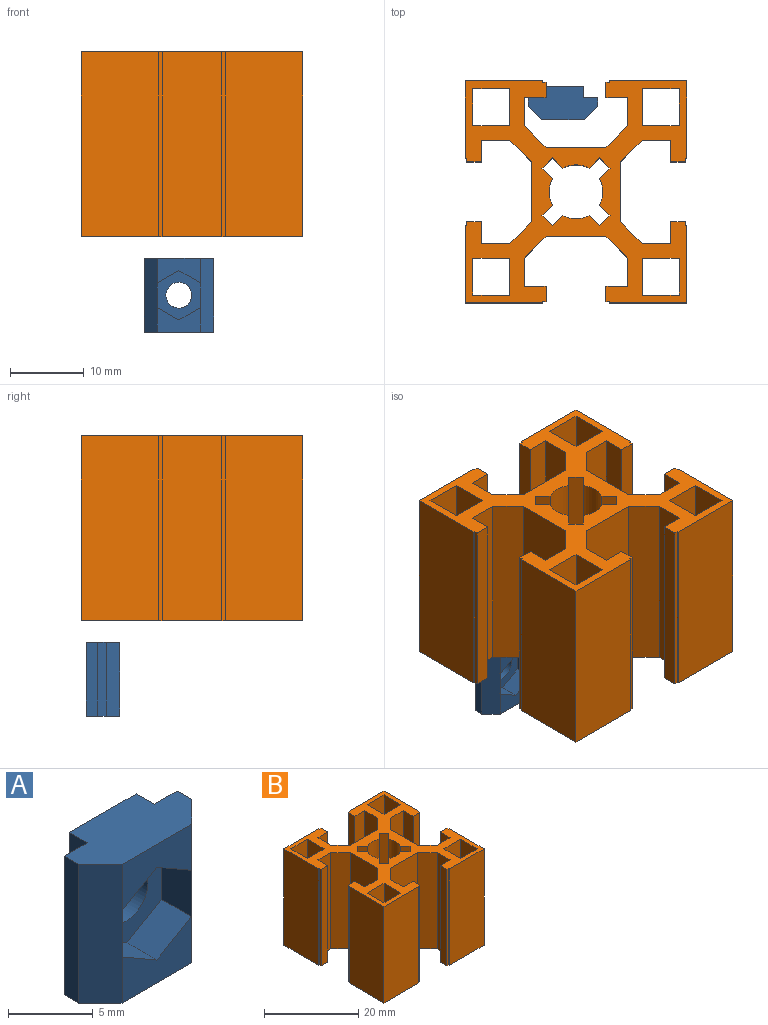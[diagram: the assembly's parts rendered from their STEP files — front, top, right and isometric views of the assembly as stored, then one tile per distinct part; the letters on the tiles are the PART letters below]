
ASSEMBLY  parts=2 mates=1
PART A: 21 faces, bbox 9.4x4.5x10 mm
  f0: plane 5.8x3.33mm, normal (0,-1,0), area 14.4mm2, adj f6,f8,f13,f17,f18
  f1: cylinder r=1.75mm len=3.5mm, axis (0,1,0), area 22mm2, adj f2,f14
  f2: plane 10x5.55mm, normal (0,1,0), area 45.9mm2, adj f1,f3,f11,f12,f13
  f3: plane 10x1.5mm, normal (-1,0.02,0), area 15mm2, adj f2,f4,f12,f13
  f4: plane 10x1.9mm, normal (0,1,0), area 19mm2, adj f3,f5,f12,f13
  f5: plane 10x1.2mm, normal (-1,0,0), area 12mm2, adj f4,f6,f12,f13
  f6: plane 10x1.8mm, normal (-0.71,-0.71,0), area 25.5mm2, adj f0,f5,f7,f12,f13,f16
  f7: plane 5.8x3.33mm, normal (0,-1,0), area 14.4mm2, adj f6,f8,f12,f15,f20
  f8: plane 10x1.8mm, normal (0.71,-0.71,0), area 25.5mm2, adj f0,f7,f9,f12,f13,f19
  f9: plane 10x1.2mm, normal (1,0,0), area 12mm2, adj f8,f10,f12,f13
  f10: plane 10x1.9mm, normal (0,1,0), area 19mm2, adj f9,f11,f12,f13
  f11: plane 10x1.5mm, normal (1,0.02,0), area 15mm2, adj f2,f10,f12,f13
  f12: plane 9.4x4.5mm, normal (0,0,1), area 33.3mm2, adj f2,f3,f4,f5,f6,f7,f8,f9
  f13: plane 9.4x4.5mm, normal (0,0,-1), area 33.3mm2, adj f0,f2,f3,f4,f5,f6,f8,f9
  f14: plane 6.7x5.8mm, normal (0,-1,0), area 19.5mm2, adj f1,f15,f16,f17,f18,f19,f20
  f15: plane 2.9x2.5mm, normal (0.5,0,-0.87), area 8.4mm2, adj f7,f14,f16,f20
  f16: plane 3.35x2.5mm, normal (1,0,0), area 8.4mm2, adj f6,f14,f15,f17
  f17: plane 2.9x2.5mm, normal (0.5,0,0.87), area 8.4mm2, adj f0,f14,f16,f18
  f18: plane 2.9x2.5mm, normal (-0.5,0,0.87), area 8.4mm2, adj f0,f14,f17,f19
  f19: plane 3.35x2.5mm, normal (-1,0,0), area 8.4mm2, adj f8,f14,f18,f20
  f20: plane 2.9x2.5mm, normal (-0.5,0,-0.87), area 8.4mm2, adj f7,f14,f15,f19
PART B: 94 faces, bbox 30x30x25 mm
  f0: cylinder r=3.65mm len=25mm, axis (0,0,-1), area 92.7mm2, adj f1,f91,f92,f93
  f1: plane 25x1.41mm, normal (0.71,-0.71,0), area 50mm2, adj f0,f2,f92,f93
  f2: plane 25x1.41mm, normal (-0.71,-0.71,0), area 50mm2, adj f1,f3,f92,f93
  f3: plane 25x1.41mm, normal (-0.71,0.71,0), area 50mm2, adj f2,f4,f92,f93
  f4: cylinder r=3.65mm len=25mm, axis (0,0,-1), area 92.7mm2, adj f3,f5,f92,f93
  f5: plane 25x1.41mm, normal (-0.71,-0.71,0), area 50mm2, adj f4,f6,f92,f93
  f6: plane 25x1.41mm, normal (-0.71,0.71,0), area 50mm2, adj f5,f7,f92,f93
  f7: plane 25x1.41mm, normal (0.71,0.71,0), area 50mm2, adj f6,f8,f92,f93
  f8: cylinder r=3.65mm len=25mm, axis (0,0,-1), area 92.7mm2, adj f7,f9,f92,f93
  f9: plane 25x1.41mm, normal (-0.71,0.71,0), area 50mm2, adj f8,f10,f92,f93
  f10: plane 25x1.41mm, normal (0.71,0.71,0), area 50mm2, adj f9,f11,f92,f93
  f11: plane 25x1.41mm, normal (0.71,-0.71,0), area 50mm2, adj f10,f12,f92,f93
  f12: cylinder r=3.65mm len=25mm, axis (0,0,-1), area 92.7mm2, adj f11,f13,f92,f93
  f13: plane 25x1.41mm, normal (0.71,0.71,0), area 50mm2, adj f12,f14,f92,f93
  f14: plane 25x1.41mm, normal (0.71,-0.71,0), area 50mm2, adj f13,f91,f92,f93
  f15: plane 25x3.85mm, normal (-1,0,0), area 96.3mm2, adj f16,f86,f92,f93
  f16: plane 25x2.95mm, normal (0,1,0), area 73.8mm2, adj f15,f17,f92,f93
  f17: plane 25x2mm, normal (-1,0,0), area 50mm2, adj f16,f18,f92,f93
  f18: plane 25x0.5mm, normal (0,-1,0), area 12.5mm2, adj f17,f19,f92,f93
  f19: plane 25x0.2mm, normal (-1,0,0), area 5mm2, adj f18,f20,f92,f93
  f20: plane 25x10.45mm, normal (0,-1,0), area 261.2mm2, adj f19,f21,f92,f93
  f21: plane 25x10.45mm, normal (1,0,0), area 261.2mm2, adj f20,f22,f92,f93
  f22: plane 25x0.2mm, normal (0,1,0), area 5mm2, adj f21,f23,f92,f93
  f23: plane 25x0.5mm, normal (1,0,0), area 12.5mm2, adj f22,f24,f92,f93
  f24: plane 25x2mm, normal (0,1,0), area 50mm2, adj f23,f25,f92,f93
  f25: plane 25x2.95mm, normal (-1,0,0), area 73.8mm2, adj f24,f26,f92,f93
  f26: plane 25x3.85mm, normal (0,1,0), area 96.3mm2, adj f25,f27,f92,f93
  f27: plane 25x2.95mm, normal (0.71,0.71,0), area 104.3mm2, adj f26,f28,f92,f93
  f28: plane 25x8.1mm, normal (1,0,0), area 202.5mm2, adj f27,f29,f92,f93
  f29: plane 25x2.95mm, normal (0.71,-0.71,0), area 104.3mm2, adj f28,f30,f92,f93
  f30: plane 25x3.85mm, normal (0,-1,0), area 96.3mm2, adj f29,f31,f92,f93
  f31: plane 25x2.95mm, normal (-1,0,0), area 73.8mm2, adj f30,f32,f92,f93
  f32: plane 25x2mm, normal (0,-1,0), area 50mm2, adj f31,f33,f92,f93
  f33: plane 25x0.5mm, normal (1,0,0), area 12.5mm2, adj f32,f34,f92,f93
  f34: plane 25x0.2mm, normal (0,-1,0), area 5mm2, adj f33,f35,f92,f93
  f35: plane 25x10.45mm, normal (1,0,0), area 261.2mm2, adj f34,f36,f92,f93
  f36: plane 25x10.45mm, normal (0,1,0), area 261.2mm2, adj f35,f37,f92,f93
  f37: plane 25x0.2mm, normal (-1,0,0), area 5mm2, adj f36,f38,f92,f93
  f38: plane 25x0.5mm, normal (0,1,0), area 12.5mm2, adj f37,f39,f92,f93
  f39: plane 25x2mm, normal (-1,0,0), area 50mm2, adj f38,f40,f92,f93
  f40: plane 25x2.95mm, normal (0,-1,0), area 73.8mm2, adj f39,f41,f92,f93
  f41: plane 25x3.85mm, normal (-1,0,0), area 96.3mm2, adj f40,f42,f92,f93
  f42: plane 25x2.95mm, normal (-0.71,0.71,0), area 104.3mm2, adj f41,f43,f92,f93
  f43: plane 25x8.1mm, normal (0,1,0), area 202.5mm2, adj f42,f44,f92,f93
  f44: plane 25x2.95mm, normal (0.71,0.71,0), area 104.3mm2, adj f43,f45,f92,f93
  f45: plane 25x3.85mm, normal (1,0,0), area 96.3mm2, adj f44,f46,f92,f93
  f46: plane 25x2.95mm, normal (0,-1,0), area 73.8mm2, adj f45,f47,f92,f93
  f47: plane 25x2mm, normal (1,0,0), area 50mm2, adj f46,f48,f92,f93
  f48: plane 25x0.5mm, normal (0,1,0), area 12.5mm2, adj f47,f49,f92,f93
  f49: plane 25x0.2mm, normal (1,0,0), area 5mm2, adj f48,f50,f92,f93
  f50: plane 25x10.45mm, normal (0,1,0), area 261.2mm2, adj f49,f51,f92,f93
  f51: plane 25x10.45mm, normal (-1,0,0), area 261.2mm2, adj f50,f52,f92,f93
  f52: plane 25x0.2mm, normal (0,-1,0), area 5mm2, adj f51,f53,f92,f93
  f53: plane 25x0.5mm, normal (-1,0,0), area 12.5mm2, adj f52,f54,f92,f93
  f54: plane 25x2mm, normal (0,-1,0), area 50mm2, adj f53,f55,f92,f93
  f55: plane 25x2.95mm, normal (1,0,0), area 73.8mm2, adj f54,f56,f92,f93
  f56: plane 25x3.85mm, normal (0,-1,0), area 96.3mm2, adj f55,f57,f92,f93
  f57: plane 25x2.95mm, normal (-0.71,-0.71,0), area 104.3mm2, adj f56,f58,f92,f93
  f58: plane 25x8.1mm, normal (-1,0,0), area 202.5mm2, adj f57,f59,f92,f93
  f59: plane 25x2.95mm, normal (-0.71,0.71,0), area 104.3mm2, adj f58,f60,f92,f93
  f60: plane 25x3.85mm, normal (0,1,0), area 96.3mm2, adj f59,f61,f92,f93
  f61: plane 25x2.95mm, normal (1,0,0), area 73.8mm2, adj f60,f62,f92,f93
  f62: plane 25x2mm, normal (0,1,0), area 50mm2, adj f61,f63,f92,f93
  f63: plane 25x0.5mm, normal (-1,0,0), area 12.5mm2, adj f62,f64,f92,f93
  f64: plane 25x0.2mm, normal (0,1,0), area 5mm2, adj f63,f65,f92,f93
  f65: plane 25x10.45mm, normal (-1,0,0), area 261.2mm2, adj f64,f66,f92,f93
  f66: plane 25x10.45mm, normal (0,-1,0), area 261.2mm2, adj f65,f67,f92,f93
  f67: plane 25x0.2mm, normal (1,0,0), area 5mm2, adj f66,f68,f92,f93
  f68: plane 25x0.5mm, normal (0,-1,0), area 12.5mm2, adj f67,f69,f92,f93
  f69: plane 25x2mm, normal (1,0,0), area 50mm2, adj f68,f70,f92,f93
  f70: plane 25x2.95mm, normal (0,1,0), area 73.8mm2, adj f69,f71,f92,f93
  f71: plane 25x3.85mm, normal (1,0,0), area 96.3mm2, adj f70,f72,f92,f93
  f72: plane 25x2.95mm, normal (0.71,-0.71,0), area 104.3mm2, adj f71,f73,f92,f93
  f73: plane 25x8.1mm, normal (0,-1,0), area 202.5mm2, adj f72,f86,f92,f93
  f74: plane 25x5mm, normal (0,-1,0), area 125mm2, adj f75,f87,f92,f93
  f75: plane 25x5mm, normal (-1,0,0), area 125mm2, adj f74,f76,f92,f93
  f76: plane 25x5mm, normal (0,1,0), area 125mm2, adj f75,f87,f92,f93
  f77: plane 25x5mm, normal (-1,0,0), area 125mm2, adj f78,f88,f92,f93
  f78: plane 25x5mm, normal (0,1,0), area 125mm2, adj f77,f79,f92,f93
  f79: plane 25x5mm, normal (1,0,0), area 125mm2, adj f78,f88,f92,f93
  f80: plane 25x5mm, normal (0,1,0), area 125mm2, adj f81,f89,f92,f93
  f81: plane 25x5mm, normal (1,0,0), area 125mm2, adj f80,f82,f92,f93
  f82: plane 25x5mm, normal (0,-1,0), area 125mm2, adj f81,f89,f92,f93
  f83: plane 25x5mm, normal (0,1,0), area 125mm2, adj f84,f90,f92,f93
  f84: plane 25x5mm, normal (1,0,0), area 125mm2, adj f83,f85,f92,f93
  f85: plane 25x5mm, normal (0,-1,0), area 125mm2, adj f84,f90,f92,f93
  f86: plane 25x2.95mm, normal (-0.71,-0.71,0), area 104.3mm2, adj f15,f73,f92,f93
  f87: plane 25x5mm, normal (1,0,0), area 125mm2, adj f74,f76,f92,f93
  f88: plane 25x5mm, normal (0,-1,0), area 125mm2, adj f77,f79,f92,f93
  f89: plane 25x5mm, normal (-1,0,0), area 125mm2, adj f80,f82,f92,f93
  f90: plane 25x5mm, normal (-1,0,0), area 125mm2, adj f83,f85,f92,f93
  f91: plane 25x1.41mm, normal (-0.71,-0.71,0), area 50mm2, adj f0,f14,f92,f93
  f92: plane 30x30mm, normal (0,0,1), area 324.8mm2, adj f0,f1,f2,f3,f4,f5,f6,f7
  f93: plane 30x30mm, normal (0,0,-1), area 324.8mm2, adj f0,f1,f2,f3,f4,f5,f6,f7
PLACE A t=(-1.77,9.8,-12.93)mm
PLACE B at identity fixed
MATE slider A.f12 <-> B.f92  axis (0,0,1) through (-5.52,12.8,-2.93)mm
